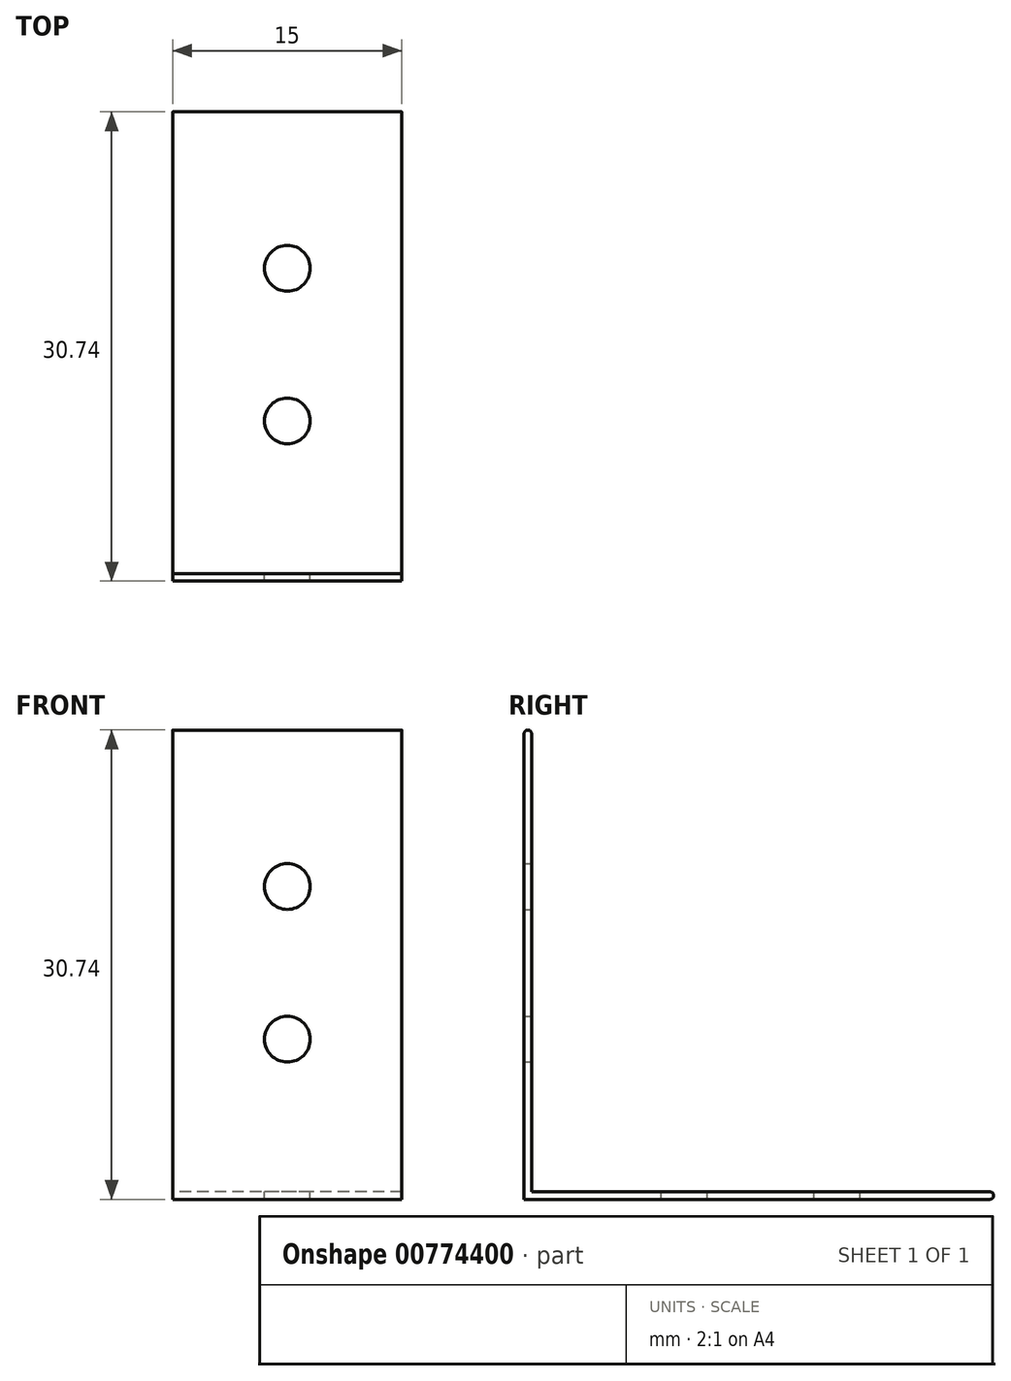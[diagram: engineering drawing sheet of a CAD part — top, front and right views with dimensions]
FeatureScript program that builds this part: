
annotation { "Feature Type Name" : "Feature", "Feature Type Description" : "" }
export const myFeature = defineFeature(function(context is Context, id is Id, definition is map)
    precondition{}
    {
        {
            var Q0;
            Q0=qCreatedBy(makeId("Right.planeOp"),FACE);
            var sketch = newSketch(context, id + "F0", { "sketchPlane" : qUnion([Q0])});
            skLineSegment(sketch, "E0", {"start": v(0, 30) * mm, "end": v(0, 0) * mm});
            skLineSegment(sketch, "E1", {"start": v(0, 0) * mm, "end": v(30, 0) * mm});
            skLineSegment(sketch, "E2.0", {"start": v(-0.5, -0.5) * mm, "end": v(30, -0.5) * mm});
            skLineSegment(sketch, "E2.1", {"start": v(-0.5, 30) * mm, "end": v(-0.5, -0.5) * mm});
            skArc(sketch, "E3", {"start": v(30, -0.5) * mm, "mid": v(30.25, -0.25) * mm, "end": v(30, 0) * mm});
            skArc(sketch, "E4", {"start": v(0, 30) * mm, "mid": v(-0.25, 30.25) * mm, "end": v(-0.5, 30) * mm});
            skSolve(sketch);
        }
        {
            var Q0;
            Q0=makeQuery(id+"F0.imprint","IMPRINT",FACE,{"disambiguationData":[TD([[makeQuery(id+"F0.imprint","IMPRINT",EDGE,{"derivedFrom":sQuery(id+"F0.wireOp",EDGE,"E0")}),-1.0]])]});
            extrude(context, id + "F1", {"entities" : qUnion([Q0]), "depth" : 15 * mm, "offsetDistance" : 25 * mm, "symmetric" : true});
        }
        {
            var Q0;
            Q0=makeQuery(id+"F1.opExtrude","SWEPT_FACE",FACE,{"disambiguationData":[OSD([sQuery(id+"F0.wireOp",EDGE,"E0")])]});
            var sketch = newSketch(context, id + "F2", { "sketchPlane" : qUnion([Q0])});
            skCircle(sketch, "E5", {"center": v(0, 10) * mm, "radius": 1.5 * mm});
            skCircle(sketch, "E6", {"center": v(0, 20) * mm, "radius": 1.5 * mm});
            skSolve(sketch);
        }
        {
            var Q0;
            Q0=makeQuery(id+"F2.imprint","IMPRINT",FACE,{"disambiguationData":[TD([[makeQuery(id+"F2.imprint","IMPRINT",EDGE,{"derivedFrom":sQuery(id+"F2.wireOp",EDGE,"E6")}),1.0]])]});
            var Q1;
            Q1=makeQuery(id+"F2.imprint","IMPRINT",FACE,{"disambiguationData":[TD([[makeQuery(id+"F2.imprint","IMPRINT",EDGE,{"derivedFrom":sQuery(id+"F2.wireOp",EDGE,"E5")}),1.0]])]});
            extrude(context, id + "F3", {"entities" : qUnion([Q0, Q1]), "operationType" : NewBodyOperationType.REMOVE, "endBound" : BoundingType.THROUGH_ALL, "oppositeDirection" : true, "depth" : 25 * mm, "offsetDistance" : 25 * mm});
        }
        {
            var Q0;
            Q0=makeQuery(id+"F1.opExtrude","SWEPT_FACE",FACE,{"disambiguationData":[OSD([sQuery(id+"F0.wireOp",EDGE,"E1")])]});
            var sketch = newSketch(context, id + "F4", { "sketchPlane" : qUnion([Q0])});
            skCircle(sketch, "E7", {"center": v(0, 20) * mm, "radius": 1.5 * mm});
            skCircle(sketch, "E8", {"center": v(0, 10) * mm, "radius": 1.5 * mm});
            skSolve(sketch);
        }
        {
            var Q0;
            Q0=makeQuery(id+"F4.imprint","IMPRINT",FACE,{"disambiguationData":[TD([[makeQuery(id+"F4.imprint","IMPRINT",EDGE,{"derivedFrom":sQuery(id+"F4.wireOp",EDGE,"E7")}),1.0]])]});
            var Q1;
            Q1=makeQuery(id+"F4.imprint","IMPRINT",FACE,{"disambiguationData":[TD([[makeQuery(id+"F4.imprint","IMPRINT",EDGE,{"derivedFrom":sQuery(id+"F4.wireOp",EDGE,"E8")}),1.0]])]});
            extrude(context, id + "F5", {"entities" : qUnion([Q0, Q1]), "operationType" : NewBodyOperationType.REMOVE, "endBound" : BoundingType.THROUGH_ALL, "oppositeDirection" : true, "depth" : 25 * mm, "offsetDistance" : 25 * mm});
        }
    });
